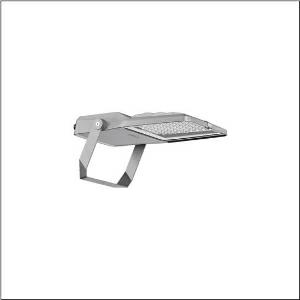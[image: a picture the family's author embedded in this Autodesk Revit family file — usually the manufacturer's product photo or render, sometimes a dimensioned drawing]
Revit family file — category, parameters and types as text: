
# Revit family: floodlight_fl_21_mini___pl52_5xa7776b2d1a_de24
name_source: partatom
category: Lighting Fixtures
units: mm (PartAtom-declared; Revit-internal decimal feet)

## family parameters
Cut with Voids When Loaded = No
Host = Face
Light Source = No
Part Type = Normal
Room Calculation Point = No
Round Connector Dimension = Use Diameter
Shared = No

## types (1)
- --- (1 x LED, 6230 lm, 45.7 W, 3000K)
    Apparent Load = 46 VA
    CIE Flux Codes = 26 60 98 100 100
    Color Rendering = 70
    Color Temperature = 3000K
    Default Elevation = 1800 mm
    Description = Floodlight FL 21 mini, floodlight, primary light control with lens, of PMMA, primary optical cover: protective disc, of toughened safety glass, transparent, light distribution: PL52, light emission: direct distribution, installation type: surface-mounted, LED, High Power LED, rated luminous flux: 6.230lm, luminous efficacy: 136lm/W, light colour: 730, colour temperature: 3000K, control gear: Smart Interface (Zhaga), control: flexible luminous flux parameterisation, time-dependent luminous flux control, constant luminous flux control, overheat protection, pre-setting: logarithmic dimming characteristic, with terminal, 6-pole, mains connection: 220..240V, AC, 50/60Hz, start of lifetime: 46W, end of service life: 48W, reduction: 22W, luminaire housing, of diecast aluminium, powder-coated, Siteco® metallic grey (DB 702S), corrosivity category C5 mid according to DIN EN ISO 12944, suitable for swimming pools, chlorine-resistant, sealing non-destructively replaceable, mounting bracket, of steel, galvanised, powder-coated, Siteco® metallic grey (DB 702S), Smart Interface below and above, protection rating (complete): IP66, insulation class (complete): insulation class II (safety insulation), certification: CE, ENEC, VDE, protection symbol: D, impact resistance: IK08, permissible operating ambient temperature: -40..+40°C, permissible operating ambient temperature for outdoor applications: -40..+50°C, standard: DIN EN 12944, LABS conformity tested according to VDMA 24364:2018-05, packaging unit: 1 piece

Light Distribution: PL52
    Height = 70 mm
    Lamp = 1 x LED
    Lamp Light Flux = 6230 lm
    Lamp Power = 45.7 W
    Lamp count = 1
    Length = 485 mm
    Luminous efficacy = 136 lm/W
    Manufacturer = Siteco
    ModVariant = No
    Model = 5XA7776B2D1A
    Number of Poles = 1
    OnlyDefault = Yes
    Power Factor = 1
    Product Name = Floodlight FL 21 mini | PL52
    Product group = floodlight | pylon annexe
    ProductGroupID = 6200
    Protection Class = Protection class II
    Protection Degree = IP 66
    RLX_Detail_Level = 1
    RLX_Emergency_Light_Flux = 0 lm
    RLX_Emergency_Type = 0
    RLX_Emergency_Type_DB = No
    RlxData = <blob elided: 96161 chars, md5=ed3c122b>
    Socket = socket
    Standby Power = 0 W
    System Light Flux = 6230 lm
    System Power = 46 W
    Type Comments = factory setting: luminous flux: 100 % | dim-lin: 254 | 463 mA
    Type Image = l_1006845.jpg
    URL = http://relux.com
    VarID = @adj_163420
    Voltage = 0 V
    Weight = 0.00 kg
    Width = 337 mm

## geometry (parser evidence)
native form markers: Blend x4, Sweep x14
no freeform markers — native parametric forms only
